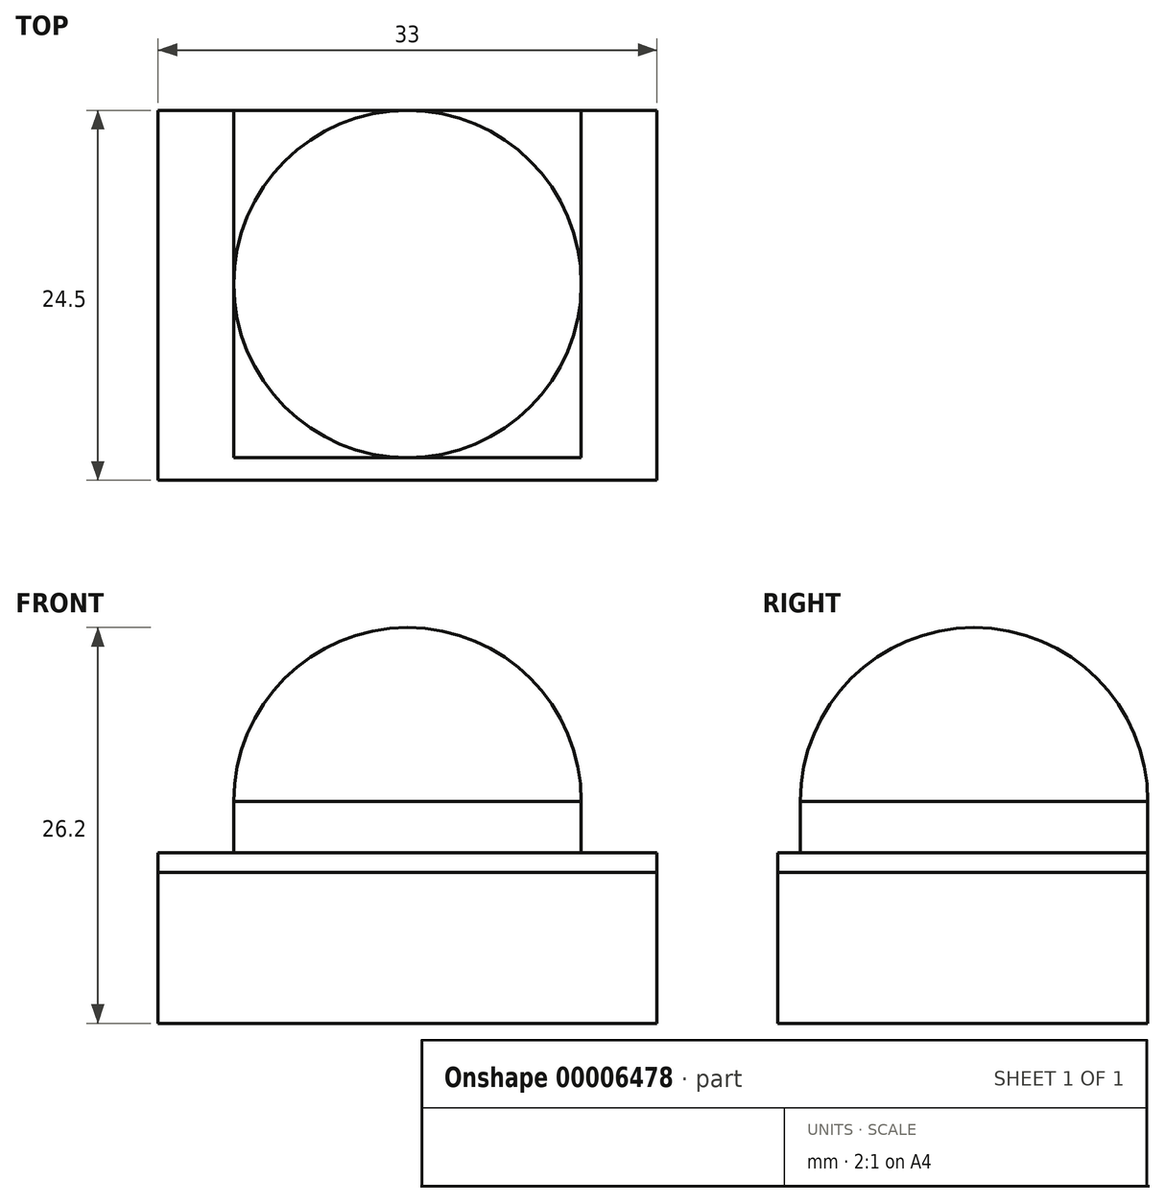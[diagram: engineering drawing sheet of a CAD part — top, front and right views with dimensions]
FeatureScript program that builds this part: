
annotation { "Feature Type Name" : "Feature", "Feature Type Description" : "" }
export const myFeature = defineFeature(function(context is Context, id is Id, definition is map)
    precondition{}
    {
        {
            var Q0;
            Q0=qCreatedBy(makeId("Top.planeOp"),FACE);
            var sketch = newSketch(context, id + "F0", { "sketchPlane" : qUnion([Q0])});
            skLineSegment(sketch, "E0.bottom", {"start": v(0, 0) * mm, "end": v(-33, 0) * mm});
            skLineSegment(sketch, "E0.top", {"start": v(0, -24.5) * mm, "end": v(-33, -24.5) * mm});
            skLineSegment(sketch, "E0.left", {"start": v(0, 0) * mm, "end": v(0, -24.5) * mm});
            skLineSegment(sketch, "E0.right", {"start": v(-33, 0) * mm, "end": v(-33, -24.5) * mm});
            skLineSegment(sketch, "E1.bottom", {"start": v(-5, 0) * mm, "end": v(-28, 0) * mm});
            skLineSegment(sketch, "E1.top", {"start": v(-5, -23) * mm, "end": v(-28, -23) * mm});
            skLineSegment(sketch, "E1.left", {"start": v(-5, 0) * mm, "end": v(-5, -23) * mm});
            skLineSegment(sketch, "E1.right", {"start": v(-28, 0) * mm, "end": v(-28, -23) * mm});
            skArc(sketch, "E2", {"start": v(-16.5, -23) * mm, "mid": v(-5, -11.5) * mm, "end": v(-16.5, 0) * mm});
            skLineSegment(sketch, "E3", {"start": v(-16.5, 0) * mm, "end": v(-16.5, -24.5) * mm, "construction": true});
            skLineSegment(sketch, "E4", {"start": v(-16.5, 0) * mm, "end": v(-16.5, -23) * mm});
            skSolve(sketch);
        }
        {
            var Q0;
            Q0=makeQuery(id+"F0.imprint","IMPRINT",FACE,{"disambiguationData":[TD([[makeQuery(id+"F0.imprint","IMPRINT",EDGE,{"derivedFrom":sQuery(id+"F0.wireOp",EDGE,"E0.top")}),-1.0]])]});
            var Q1;
            {var subQ1=sQuery(id+"F0.wireOp",EDGE,"E1.left");var subQ3=sQuery(id+"F0.wireOp",EDGE,"E1.top");var subQ5=makeQuery(id+"F0.imprint","INTERSECT",VERTEX,{"derivedFrom":[subQ3,subQ1]});Q1=makeQuery(id+"F0.imprint","IMPRINT",FACE,{"disambiguationData":[TD([[makeQuery(id+"F0.imprint","IMPRINT",EDGE,{"disambiguationData":[TD([[subQ5,1.0]])],"derivedFrom":subQ1}),-1.0]])]});}
            var Q2;
            {var subQ0=sQuery(id+"F0.wireOp",EDGE,"E4");Q2=makeQuery(id+"F0.imprint","IMPRINT",FACE,{"disambiguationData":[TD([[makeQuery(id+"F0.imprint","IMPRINT",EDGE,{"derivedFrom":subQ0}),1.0]])]});}
            var Q3;
            {var subQ0=sQuery(id+"F0.wireOp",EDGE,"E2");var subQ1=sQuery(id+"F0.wireOp",EDGE,"E1.left");var subQ2=makeQuery(id+"F0.imprint","INTERSECT",VERTEX,{"derivedFrom":[subQ1,subQ0]});Q3=makeQuery(id+"F0.imprint","IMPRINT",FACE,{"disambiguationData":[TD([[makeQuery(id+"F0.imprint","IMPRINT",EDGE,{"disambiguationData":[TD([[subQ2,1.0]])],"derivedFrom":subQ1}),-1.0]])]});}
            var Q4;
            {var subQ1=sQuery(id+"F0.wireOp",EDGE,"E1.right");Q4=makeQuery(id+"F0.imprint","IMPRINT",FACE,{"disambiguationData":[TD([[makeQuery(id+"F0.imprint","IMPRINT",EDGE,{"derivedFrom":subQ1}),1.0]])]});}
            extrude(context, id + "F1", {"entities" : qUnion([Q0, Q1, Q2, Q3, Q4]), "oppositeDirection" : true, "depth" : 1.3 * mm});
        }
        {
            var Q0;
            {var subQ1=sQuery(id+"F0.wireOp",EDGE,"E1.right");Q0=makeQuery(id+"F0.imprint","IMPRINT",FACE,{"disambiguationData":[TD([[makeQuery(id+"F0.imprint","IMPRINT",EDGE,{"derivedFrom":subQ1}),1.0]])]});}
            var Q1;
            {var subQ0=sQuery(id+"F0.wireOp",EDGE,"E4");Q1=makeQuery(id+"F0.imprint","IMPRINT",FACE,{"disambiguationData":[TD([[makeQuery(id+"F0.imprint","IMPRINT",EDGE,{"derivedFrom":subQ0}),1.0]])]});}
            var Q2;
            {var subQ1=sQuery(id+"F0.wireOp",EDGE,"E1.left");var subQ3=sQuery(id+"F0.wireOp",EDGE,"E1.top");var subQ5=makeQuery(id+"F0.imprint","INTERSECT",VERTEX,{"derivedFrom":[subQ3,subQ1]});Q2=makeQuery(id+"F0.imprint","IMPRINT",FACE,{"disambiguationData":[TD([[makeQuery(id+"F0.imprint","IMPRINT",EDGE,{"disambiguationData":[TD([[subQ5,1.0]])],"derivedFrom":subQ1}),-1.0]])]});}
            var Q3;
            {var subQ0=sQuery(id+"F0.wireOp",EDGE,"E2");var subQ1=sQuery(id+"F0.wireOp",EDGE,"E1.left");var subQ2=makeQuery(id+"F0.imprint","INTERSECT",VERTEX,{"derivedFrom":[subQ1,subQ0]});Q3=makeQuery(id+"F0.imprint","IMPRINT",FACE,{"disambiguationData":[TD([[makeQuery(id+"F0.imprint","IMPRINT",EDGE,{"disambiguationData":[TD([[subQ2,1.0]])],"derivedFrom":subQ1}),-1.0]])]});}
            extrude(context, id + "F2", {"entities" : qUnion([Q0, Q1, Q2, Q3]), "depth" : (4.7 - 1.3) * mm});
        }
        {
            var Q0;
            Q0=makeQuery(id+"F2.opExtrude","CAP_FACE",FACE,{"disambiguationData":[OSD([sQuery(id+"F0.wireOp",EDGE,"E1.bottom"),sQuery(id+"F0.wireOp",EDGE,"E1.top"),sQuery(id+"F0.wireOp",EDGE,"E1.left"),sQuery(id+"F0.wireOp",EDGE,"E1.right")])],"isStart":false});
            var sketch = newSketch(context, id + "F3", { "sketchPlane" : qUnion([Q0])});
            skArc(sketch, "E5.0", {"start": v(-16.5, -23) * mm, "mid": v(-5, -11.5) * mm, "end": v(-16.5, 0) * mm});
            skLineSegment(sketch, "E6.0", {"start": v(-16.5, 0) * mm, "end": v(-16.5, -23) * mm});
            skSolve(sketch);
        }
        {
            var Q0;
            {var subQ0=sQuery(id+"F3.wireOp",EDGE,"E6.0");Q0=makeQuery(id+"F3.imprint","IMPRINT",FACE,{"disambiguationData":[TD([[makeQuery(id+"F3.imprint","IMPRINT",EDGE,{"derivedFrom":subQ0}),1.0]])]});}
            var Q1;
            Q1=sQuery(id+"F3.wireOp",EDGE,"E6.0");
            revolve(context, id + "F4", {"operationType" : NewBodyOperationType.ADD, "entities" : qUnion([Q0]), "axis" : qUnion([Q1]), "revolveType" : RevolveType.ONE_DIRECTION, "angle" : 180 * degree});
        }
        {
            var Q0;
            Q0=makeQuery(id+"F1.opExtrude","CAP_FACE",FACE,{"disambiguationData":[OSD([sQuery(id+"F0.wireOp",EDGE,"E0.bottom"),sQuery(id+"F0.wireOp",EDGE,"E0.top"),sQuery(id+"F0.wireOp",EDGE,"E0.left"),sQuery(id+"F0.wireOp",EDGE,"E0.right"),sQuery(id+"F0.wireOp",EDGE,"E1.bottom")])],"isStart":false});
            extrude(context, id + "F5", {"entities" : qUnion([Q0]), "depth" : 10 * mm});
        }
    });
